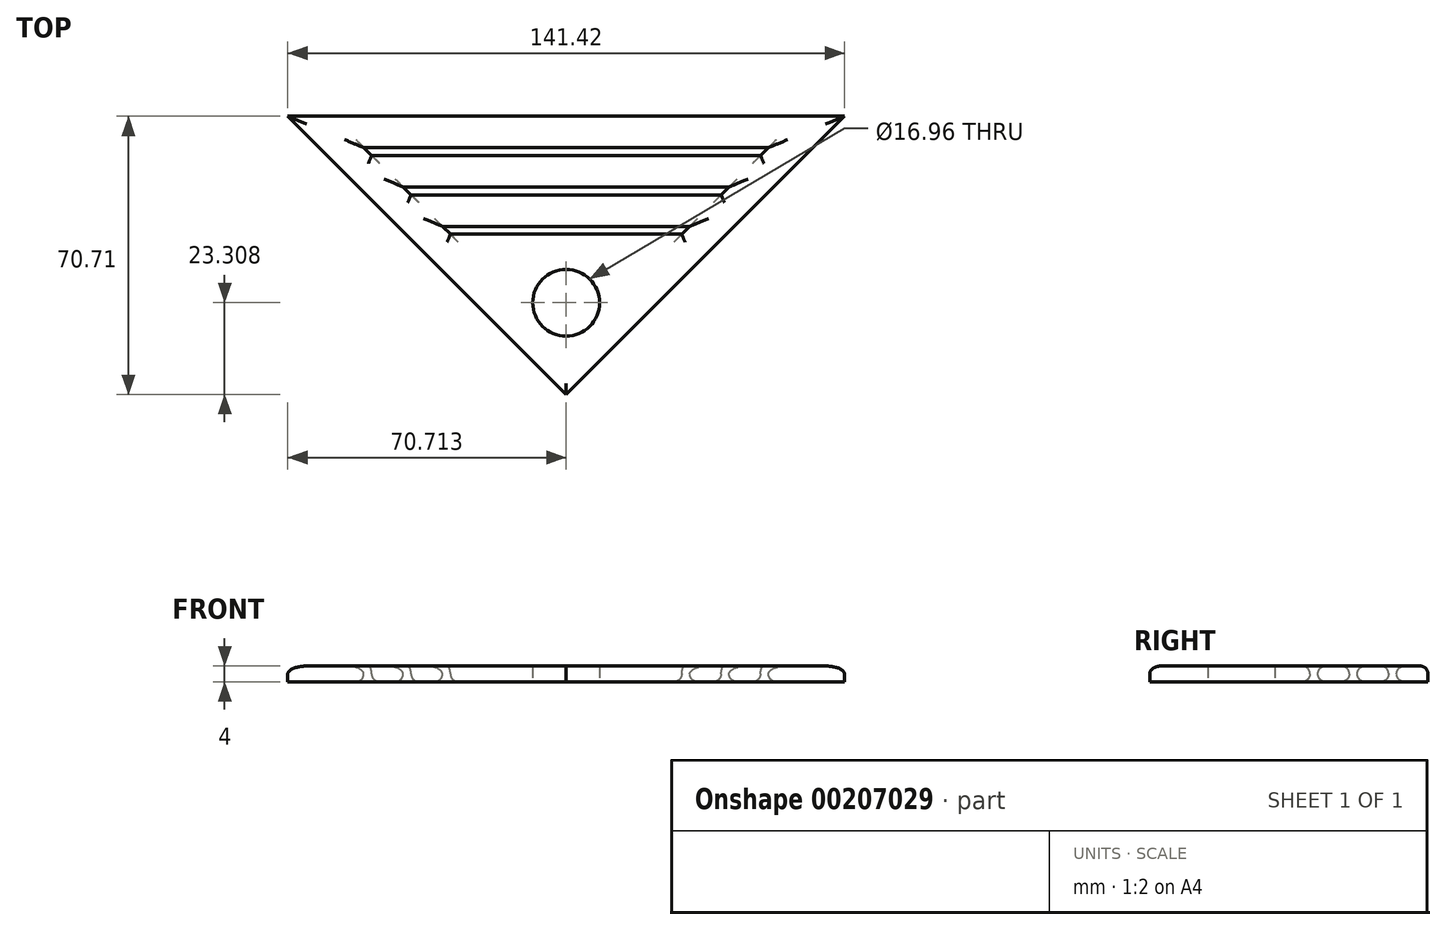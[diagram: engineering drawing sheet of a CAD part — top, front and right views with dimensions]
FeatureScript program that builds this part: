
annotation { "Feature Type Name" : "Feature", "Feature Type Description" : "" }
export const myFeature = defineFeature(function(context is Context, id is Id, definition is map)
    precondition{}
    {
        {
            var Q0;
            Q0=qCreatedBy(makeId("Top.planeOp"),FACE);
            var sketch = newSketch(context, id + "F0", { "sketchPlane" : qUnion([Q0])});
            skLineSegment(sketch, "E0", {"start": v(-31.6, 35.93) * mm, "end": v(-31.6, -34.78) * mm});
            skLineSegment(sketch, "E1", {"start": v(-31.6, -34.78) * mm, "end": v(39.11, 35.93) * mm});
            skLineSegment(sketch, "E2", {"start": v(39.11, 35.93) * mm, "end": v(-31.6, 35.93) * mm});
            skLineSegment(sketch, "E3", {"start": v(-31.6, -23.46) * mm, "end": v(27.8, 35.93) * mm});
            skLineSegment(sketch, "E4", {"start": v(-31.6, 25.93) * mm, "end": v(17.8, 25.93) * mm});
            skLineSegment(sketch, "E5", {"start": v(-31.6, 27.93) * mm, "end": v(19.8, 27.93) * mm});
            skLineSegment(sketch, "E6", {"start": v(-31.6, 17.93) * mm, "end": v(9.8, 17.93) * mm});
            skLineSegment(sketch, "E7", {"start": v(-31.6, 15.93) * mm, "end": v(7.8, 15.93) * mm});
            skLineSegment(sketch, "E8", {"start": v(-31.6, 7.93) * mm, "end": v(-0.2, 7.93) * mm});
            skLineSegment(sketch, "E9", {"start": v(-31.6, 5.93) * mm, "end": v(-2.2, 5.93) * mm});
            skLineSegment(sketch, "E10.MirrorCS", {"start": v(-102.3, 35.93) * mm, "end": v(-31.6, 35.93) * mm});
            skLineSegment(sketch, "E11.MirrorCS", {"start": v(-31.6, -34.78) * mm, "end": v(-102.3, 35.93) * mm});
            skLineSegment(sketch, "E12.MirrorCS", {"start": v(-31.6, -23.46) * mm, "end": v(-91, 35.93) * mm});
            skLineSegment(sketch, "E13.MirrorCS", {"start": v(-31.6, 5.93) * mm, "end": v(-61, 5.93) * mm});
            skLineSegment(sketch, "E14.MirrorCS", {"start": v(-31.6, 7.93) * mm, "end": v(-63, 7.93) * mm});
            skLineSegment(sketch, "E15.MirrorCS", {"start": v(-31.6, 15.93) * mm, "end": v(-71, 15.93) * mm});
            skLineSegment(sketch, "E16.MirrorCS", {"start": v(-31.6, 17.93) * mm, "end": v(-73, 17.93) * mm});
            skLineSegment(sketch, "E17.MirrorCS", {"start": v(-31.6, 25.93) * mm, "end": v(-81, 25.93) * mm});
            skLineSegment(sketch, "E18.MirrorCS", {"start": v(-31.6, 27.93) * mm, "end": v(-83, 27.93) * mm});
            skCircle(sketch, "E19", {"center": v(-31.6, -11.47) * mm, "radius": 8.48 * mm});
            skSolve(sketch);
        }
        {
            var Q0;
            {var subQ3=sQuery(id+"F0.wireOp",EDGE,"E11.MirrorCS");Q0=makeQuery(id+"F0.imprint","IMPRINT",FACE,{"disambiguationData":[TD([[makeQuery(id+"F0.imprint","IMPRINT",EDGE,{"derivedFrom":subQ3}),-1.0]])]});}
            var Q1;
            {var subQ0=sQuery(id+"F0.wireOp",EDGE,"E13.MirrorCS");Q1=makeQuery(id+"F0.imprint","IMPRINT",FACE,{"disambiguationData":[TD([[makeQuery(id+"F0.imprint","IMPRINT",EDGE,{"derivedFrom":subQ0}),1.0]])]});}
            var Q2;
            {var subQ1=sQuery(id+"F0.wireOp",EDGE,"E0");var subQ3=sQuery(id+"F0.wireOp",EDGE,"E19");var subQ4=makeQuery(id+"F0.imprint","INTERSECT",VERTEX,{"disambiguationData":[OD(1.0)],"derivedFrom":[subQ1,subQ3]});Q2=makeQuery(id+"F0.imprint","IMPRINT",FACE,{"disambiguationData":[TD([[makeQuery(id+"F0.imprint","IMPRINT",EDGE,{"disambiguationData":[TD([[subQ4,-1.0]])],"derivedFrom":subQ3}),-1.0]])]});}
            var Q3;
            {var subQ5=sQuery(id+"F0.wireOp",EDGE,"E1");Q3=makeQuery(id+"F0.imprint","IMPRINT",FACE,{"disambiguationData":[TD([[makeQuery(id+"F0.imprint","IMPRINT",EDGE,{"derivedFrom":subQ5}),1.0]])]});}
            var Q4;
            {var subQ1=sQuery(id+"F0.wireOp",EDGE,"E0");var subQ3=sQuery(id+"F0.wireOp",EDGE,"E19");var subQ4=makeQuery(id+"F0.imprint","INTERSECT",VERTEX,{"disambiguationData":[OD(1.0)],"derivedFrom":[subQ1,subQ3]});Q4=makeQuery(id+"F0.imprint","IMPRINT",FACE,{"disambiguationData":[TD([[makeQuery(id+"F0.imprint","IMPRINT",EDGE,{"disambiguationData":[TD([[subQ4,1.0]])],"derivedFrom":subQ3}),-1.0]])]});}
            var Q5;
            {var subQ0=sQuery(id+"F0.wireOp",EDGE,"E9");Q5=makeQuery(id+"F0.imprint","IMPRINT",FACE,{"disambiguationData":[TD([[makeQuery(id+"F0.imprint","IMPRINT",EDGE,{"derivedFrom":subQ0}),-1.0]])]});}
            var Q6;
            {var subQ0=sQuery(id+"F0.wireOp",EDGE,"E7");Q6=makeQuery(id+"F0.imprint","IMPRINT",FACE,{"disambiguationData":[TD([[makeQuery(id+"F0.imprint","IMPRINT",EDGE,{"derivedFrom":subQ0}),-1.0]])]});}
            var Q7;
            {var subQ2=sQuery(id+"F0.wireOp",EDGE,"E14.MirrorCS");Q7=makeQuery(id+"F0.imprint","IMPRINT",FACE,{"disambiguationData":[TD([[makeQuery(id+"F0.imprint","IMPRINT",EDGE,{"derivedFrom":subQ2}),-1.0]])]});}
            var Q8;
            {var subQ0=sQuery(id+"F0.wireOp",EDGE,"E4");Q8=makeQuery(id+"F0.imprint","IMPRINT",FACE,{"disambiguationData":[TD([[makeQuery(id+"F0.imprint","IMPRINT",EDGE,{"derivedFrom":subQ0}),-1.0]])]});}
            var Q9;
            {var subQ2=sQuery(id+"F0.wireOp",EDGE,"E16.MirrorCS");Q9=makeQuery(id+"F0.imprint","IMPRINT",FACE,{"disambiguationData":[TD([[makeQuery(id+"F0.imprint","IMPRINT",EDGE,{"derivedFrom":subQ2}),-1.0]])]});}
            var Q10;
            {var subQ3=sQuery(id+"F0.wireOp",EDGE,"E5");Q10=makeQuery(id+"F0.imprint","IMPRINT",FACE,{"disambiguationData":[TD([[makeQuery(id+"F0.imprint","IMPRINT",EDGE,{"derivedFrom":subQ3}),1.0]])]});}
            var Q11;
            {var subQ3=sQuery(id+"F0.wireOp",EDGE,"E18.MirrorCS");Q11=makeQuery(id+"F0.imprint","IMPRINT",FACE,{"disambiguationData":[TD([[makeQuery(id+"F0.imprint","IMPRINT",EDGE,{"derivedFrom":subQ3}),-1.0]])]});}
            extrude(context, id + "F1", {"entities" : qUnion([Q0, Q1, Q2, Q3, Q4, Q5, Q6, Q7, Q8, Q9, Q10, Q11]), "depth" : 4 * mm});
        }
        {
            var Q0;
            Q0=makeQuery(id+"F1.opExtrude","CAP_EDGE",EDGE,{"disambiguationData":[OSD([sQuery(id+"F0.wireOp",EDGE,"E2"),sQuery(id+"F0.wireOp",EDGE,"E10.MirrorCS")])],"isStart":false});
            var Q1;
            Q1=makeQuery(id+"F1.opExtrude","CAP_EDGE",EDGE,{"disambiguationData":[OSD([sQuery(id+"F0.wireOp",EDGE,"E5"),sQuery(id+"F0.wireOp",EDGE,"E18.MirrorCS")])],"isStart":false});
            var Q2;
            Q2=makeQuery(id+"F1.opExtrude","CAP_EDGE",EDGE,{"disambiguationData":[OSD([sQuery(id+"F0.wireOp",EDGE,"E4"),sQuery(id+"F0.wireOp",EDGE,"E17.MirrorCS")])],"isStart":false});
            var Q3;
            Q3=makeQuery(id+"F1.opExtrude","CAP_EDGE",EDGE,{"disambiguationData":[OSD([sQuery(id+"F0.wireOp",EDGE,"E6"),sQuery(id+"F0.wireOp",EDGE,"E16.MirrorCS")])],"isStart":false});
            var Q4;
            Q4=makeQuery(id+"F1.opExtrude","CAP_EDGE",EDGE,{"disambiguationData":[OSD([sQuery(id+"F0.wireOp",EDGE,"E7"),sQuery(id+"F0.wireOp",EDGE,"E15.MirrorCS")])],"isStart":false});
            var Q5;
            Q5=makeQuery(id+"F1.opExtrude","CAP_EDGE",EDGE,{"disambiguationData":[OSD([sQuery(id+"F0.wireOp",EDGE,"E8"),sQuery(id+"F0.wireOp",EDGE,"E14.MirrorCS")])],"isStart":false});
            var Q6;
            Q6=makeQuery(id+"F1.opExtrude","CAP_EDGE",EDGE,{"disambiguationData":[OSD([sQuery(id+"F0.wireOp",EDGE,"E9"),sQuery(id+"F0.wireOp",EDGE,"E13.MirrorCS")])],"isStart":false});
            var Q7;
            Q7=makeQuery(id+"F1.opExtrude","CAP_EDGE",EDGE,{"disambiguationData":[OSD([sQuery(id+"F0.wireOp",EDGE,"E11.MirrorCS")])],"isStart":false});
            var Q8;
            Q8=makeQuery(id+"F1.opExtrude","CAP_EDGE",EDGE,{"disambiguationData":[OSD([sQuery(id+"F0.wireOp",EDGE,"E1")])],"isStart":false});
            var Q9;
            {var subQ0=sQuery(id+"F0.wireOp",EDGE,"E3");Q9=makeQuery(id+"F1.opExtrude","CAP_EDGE",EDGE,{"disambiguationData":[OSD([subQ0]),TDD([makeQuery(id+"F0.imprint","IMPRINT",EDGE,{"disambiguationData":[TD([[makeQuery(id+"F0.imprint","INTERSECT",VERTEX,{"derivedFrom":[subQ0,sQuery(id+"F0.wireOp",EDGE,"E6")]}),1.0]])],"derivedFrom":subQ0})])],"isStart":false});}
            var Q10;
            {var subQ0=sQuery(id+"F0.wireOp",EDGE,"E3");Q10=makeQuery(id+"F1.opExtrude","CAP_EDGE",EDGE,{"disambiguationData":[OSD([subQ0]),TDD([makeQuery(id+"F0.imprint","IMPRINT",EDGE,{"disambiguationData":[TD([[makeQuery(id+"F0.imprint","INTERSECT",VERTEX,{"derivedFrom":[subQ0,sQuery(id+"F0.wireOp",EDGE,"E4")]}),-1.0]])],"derivedFrom":subQ0})])],"isStart":false});}
            var Q11;
            {var subQ0=sQuery(id+"F0.wireOp",EDGE,"E3");Q11=makeQuery(id+"F1.opExtrude","CAP_EDGE",EDGE,{"disambiguationData":[OSD([subQ0]),TDD([makeQuery(id+"F0.imprint","IMPRINT",EDGE,{"disambiguationData":[TD([[makeQuery(id+"F0.imprint","INTERSECT",VERTEX,{"derivedFrom":[subQ0,sQuery(id+"F0.wireOp",EDGE,"E8")]}),1.0]])],"derivedFrom":subQ0})])],"isStart":false});}
            var Q12;
            {var subQ0=sQuery(id+"F0.wireOp",EDGE,"E12.MirrorCS");Q12=makeQuery(id+"F1.opExtrude","CAP_EDGE",EDGE,{"disambiguationData":[OSD([subQ0]),TDD([makeQuery(id+"F0.imprint","IMPRINT",EDGE,{"disambiguationData":[TD([[makeQuery(id+"F0.imprint","INTERSECT",VERTEX,{"derivedFrom":[subQ0,sQuery(id+"F0.wireOp",EDGE,"E13.MirrorCS")]}),-1.0]])],"derivedFrom":subQ0})])],"isStart":false});}
            var Q13;
            {var subQ0=sQuery(id+"F0.wireOp",EDGE,"E12.MirrorCS");Q13=makeQuery(id+"F1.opExtrude","CAP_EDGE",EDGE,{"disambiguationData":[OSD([subQ0]),TDD([makeQuery(id+"F0.imprint","IMPRINT",EDGE,{"disambiguationData":[TD([[makeQuery(id+"F0.imprint","INTERSECT",VERTEX,{"derivedFrom":[subQ0,sQuery(id+"F0.wireOp",EDGE,"E15.MirrorCS")]}),-1.0]])],"derivedFrom":subQ0})])],"isStart":false});}
            var Q14;
            {var subQ0=sQuery(id+"F0.wireOp",EDGE,"E12.MirrorCS");Q14=makeQuery(id+"F1.opExtrude","CAP_EDGE",EDGE,{"disambiguationData":[OSD([subQ0]),TDD([makeQuery(id+"F0.imprint","IMPRINT",EDGE,{"disambiguationData":[TD([[makeQuery(id+"F0.imprint","INTERSECT",VERTEX,{"derivedFrom":[subQ0,sQuery(id+"F0.wireOp",EDGE,"E17.MirrorCS")]}),-1.0]])],"derivedFrom":subQ0})])],"isStart":false});}
            fillet(context, id + "F2", {"entities" : qUnion([Q0, Q1, Q2, Q3, Q4, Q5, Q6, Q7, Q8, Q9, Q10, Q11, Q12, Q13, Q14]), "radius" : 2 * mm, "tangentPropagation" : true, "allowEdgeOverflow" : false});
        }
        {
            var Q0;
            Q0=makeQuery(id+"F1.opExtrude","CAP_EDGE",EDGE,{"disambiguationData":[OSD([sQuery(id+"F0.wireOp",EDGE,"E5"),sQuery(id+"F0.wireOp",EDGE,"E18.MirrorCS")])],"isStart":true});
            var Q1;
            Q1=makeQuery(id+"F1.opExtrude","CAP_EDGE",EDGE,{"disambiguationData":[OSD([sQuery(id+"F0.wireOp",EDGE,"E4"),sQuery(id+"F0.wireOp",EDGE,"E17.MirrorCS")])],"isStart":true});
            var Q2;
            Q2=makeQuery(id+"F1.opExtrude","CAP_EDGE",EDGE,{"disambiguationData":[OSD([sQuery(id+"F0.wireOp",EDGE,"E8"),sQuery(id+"F0.wireOp",EDGE,"E14.MirrorCS")])],"isStart":true});
            var Q3;
            Q3=makeQuery(id+"F1.opExtrude","CAP_EDGE",EDGE,{"disambiguationData":[OSD([sQuery(id+"F0.wireOp",EDGE,"E9"),sQuery(id+"F0.wireOp",EDGE,"E13.MirrorCS")])],"isStart":true});
            var Q4;
            Q4=makeQuery(id+"F1.opExtrude","CAP_EDGE",EDGE,{"disambiguationData":[OSD([sQuery(id+"F0.wireOp",EDGE,"E6"),sQuery(id+"F0.wireOp",EDGE,"E16.MirrorCS")])],"isStart":true});
            var Q5;
            Q5=makeQuery(id+"F1.opExtrude","CAP_EDGE",EDGE,{"disambiguationData":[OSD([sQuery(id+"F0.wireOp",EDGE,"E7"),sQuery(id+"F0.wireOp",EDGE,"E15.MirrorCS")])],"isStart":true});
            fillet(context, id + "F3", {"entities" : qUnion([Q0, Q1, Q2, Q3, Q4, Q5]), "radius" : 2 * mm, "tangentPropagation" : true, "allowEdgeOverflow" : false});
        }
    });
